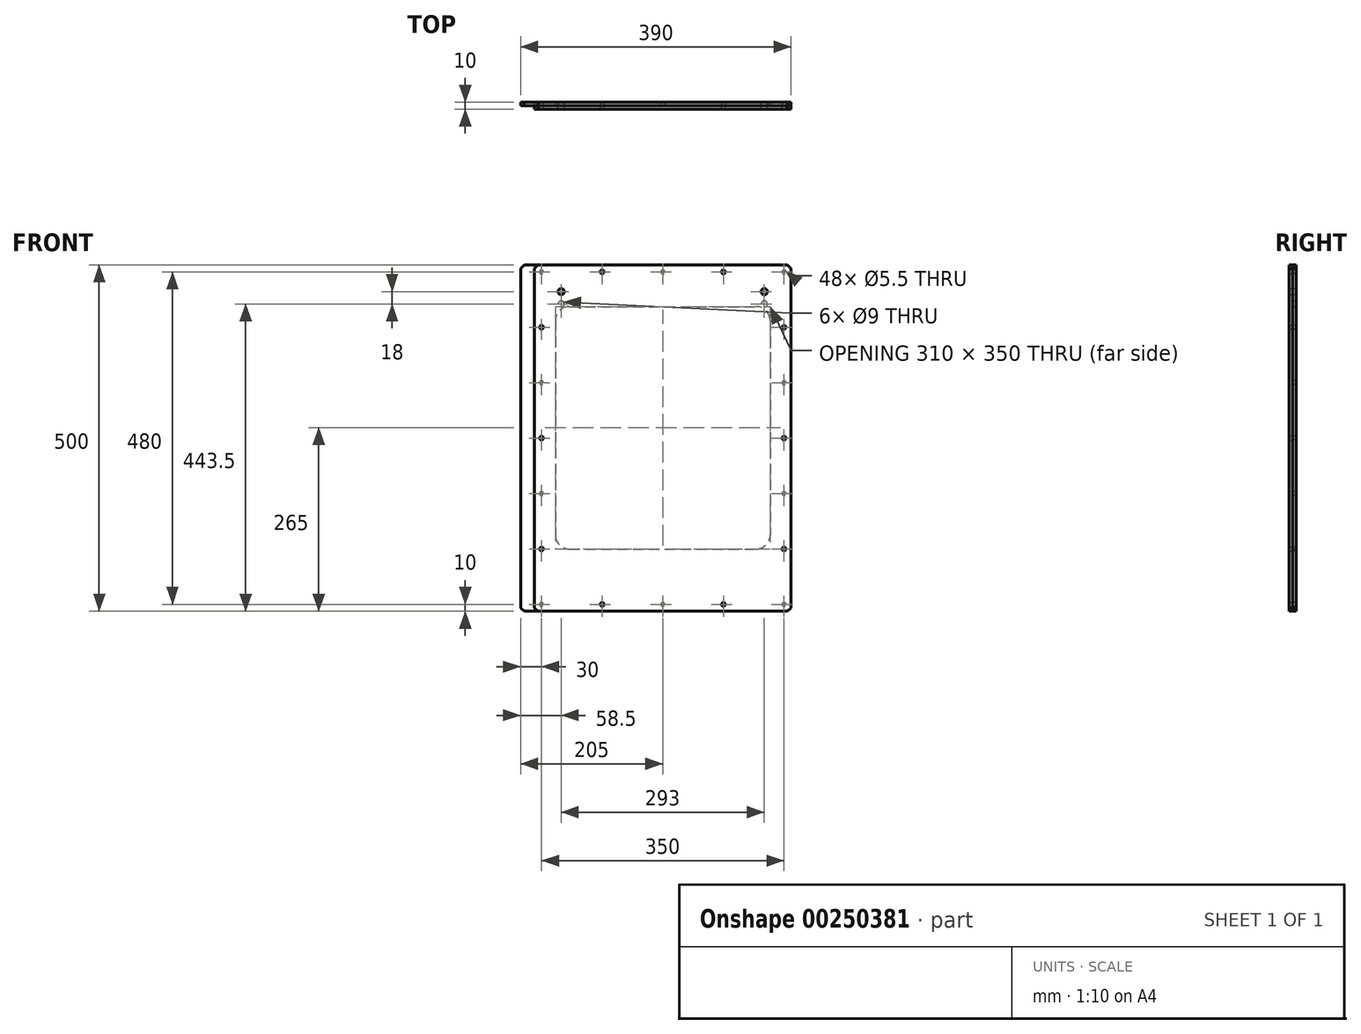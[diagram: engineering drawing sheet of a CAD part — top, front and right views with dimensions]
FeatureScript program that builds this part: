
annotation { "Feature Type Name" : "Feature", "Feature Type Description" : "" }
export const myFeature = defineFeature(function(context is Context, id is Id, definition is map)
    precondition{}
    {
        {
            var Q0;
            Q0=qCreatedBy(makeId("Front.planeOp"),FACE);
            var sketch = newSketch(context, id + "F0", { "sketchPlane" : qUnion([Q0])});
            skLineSegment(sketch, "E0.bottom", {"start": v(-175, 240) * mm, "end": v(175, 240) * mm, "construction": true});
            skLineSegment(sketch, "E0.top", {"start": v(-175, -240) * mm, "end": v(175, -240) * mm, "construction": true});
            skLineSegment(sketch, "E0.left", {"start": v(-175, 240) * mm, "end": v(-175, -240) * mm, "construction": true});
            skLineSegment(sketch, "E0.right", {"start": v(175, 240) * mm, "end": v(175, -240) * mm, "construction": true});
            skPoint(sketch, "E1", {"position": v(-175, 240) * mm});
            skPoint(sketch, "E2", {"position": v(175, 240) * mm});
            skPoint(sketch, "E3", {"position": v(-175, -240) * mm});
            skPoint(sketch, "E4", {"position": v(175, -240) * mm});
            skPoint(sketch, "E5.0.1.0", {"position": v(-175, -160) * mm});
            skPoint(sketch, "E5.0.2.0", {"position": v(-175, -80) * mm});
            skPoint(sketch, "E5.0.3.0", {"position": v(-175, 0) * mm});
            skPoint(sketch, "E5.0.4.0", {"position": v(-175, 80) * mm});
            skPoint(sketch, "E5.0.5.0", {"position": v(-175, 160) * mm});
            skPoint(sketch, "E5.1.1.0", {"position": v(175, -160) * mm});
            skPoint(sketch, "E5.1.2.0", {"position": v(175, -80) * mm});
            skPoint(sketch, "E5.1.3.0", {"position": v(175, 0) * mm});
            skPoint(sketch, "E5.1.4.0", {"position": v(175, 80) * mm});
            skPoint(sketch, "E5.1.5.0", {"position": v(175, 160) * mm});
            skLineSegment(sketch, "E5.direction2", {"start": v(-175, -240) * mm, "end": v(-175, -160) * mm, "construction": true});
            skPoint(sketch, "E6.1.0.0", {"position": v(-87.5, -240) * mm});
            skPoint(sketch, "E6.1.1.0", {"position": v(-87.5, 240) * mm});
            skPoint(sketch, "E6.2.0.0", {"position": v(0, -240) * mm});
            skPoint(sketch, "E6.2.1.0", {"position": v(0, 240) * mm});
            skPoint(sketch, "E6.3.0.0", {"position": v(87.5, -240) * mm});
            skPoint(sketch, "E6.3.1.0", {"position": v(87.5, 240) * mm});
            skLineSegment(sketch, "E6.direction1", {"start": v(-175, -240) * mm, "end": v(-87.5, -240) * mm, "construction": true});
            skLineSegment(sketch, "E6.direction2", {"start": v(-175, -240) * mm, "end": v(-175, 240) * mm, "construction": true});
            skSolve(sketch);
        }
        {
            var Q0;
            Q0=qCreatedBy(makeId("Front.planeOp"),FACE);
            var sketch = newSketch(context, id + "F1", { "sketchPlane" : qUnion([Q0])});
            skLineSegment(sketch, "E7.bottom", {"start": v(-205, 250) * mm, "end": v(185, 250) * mm});
            skLineSegment(sketch, "E7.top", {"start": v(-205, -250) * mm, "end": v(185, -250) * mm});
            skLineSegment(sketch, "E7.left", {"start": v(-205, 250) * mm, "end": v(-205, -250) * mm});
            skLineSegment(sketch, "E7.right", {"start": v(185, 250) * mm, "end": v(185, -250) * mm});
            skCircle(sketch, "E8", {"center": v(146.5, 193.5) * mm, "radius": 4.5 * mm});
            skCircle(sketch, "E9", {"center": v(-146.5, 193.5) * mm, "radius": 4.5 * mm});
            skSolve(sketch);
        }
        {
            var Q0;
            Q0=makeQuery(id+"F1.imprint","IMPRINT",FACE,{"disambiguationData":[TD([[makeQuery(id+"F1.imprint","IMPRINT",EDGE,{"derivedFrom":sQuery(id+"F1.wireOp",EDGE,"E7.bottom")}),-1.0]])]});
            extrude(context, id + "F2", {"entities" : qUnion([Q0]), "oppositeDirection" : true, "depth" : 5 * mm});
        }
        {
            var Q0;
            Q0=sQuery(id+"F0.wireOp",VERTEX,"E1");
            var Q1;
            Q1=sQuery(id+"F0.wireOp",VERTEX,"E5.0.5.0");
            var Q2;
            Q2=sQuery(id+"F0.wireOp",VERTEX,"E5.0.4.0");
            var Q3;
            Q3=sQuery(id+"F0.wireOp",VERTEX,"E5.0.2.0");
            var Q4;
            Q4=sQuery(id+"F0.wireOp",VERTEX,"E5.0.1.0");
            var Q5;
            Q5=sQuery(id+"F0.wireOp",VERTEX,"E3");
            var Q6;
            Q6=sQuery(id+"F0.wireOp",VERTEX,"E6.1.0.0");
            var Q7;
            Q7=sQuery(id+"F0.wireOp",VERTEX,"E6.3.0.0");
            var Q8;
            Q8=sQuery(id+"F0.wireOp",VERTEX,"E4");
            var Q9;
            Q9=sQuery(id+"F0.wireOp",VERTEX,"E5.1.1.0");
            var Q10;
            Q10=sQuery(id+"F0.wireOp",VERTEX,"E5.1.2.0");
            var Q11;
            Q11=sQuery(id+"F0.wireOp",VERTEX,"E5.1.4.0");
            var Q12;
            Q12=sQuery(id+"F0.wireOp",VERTEX,"E5.1.5.0");
            var Q13;
            Q13=sQuery(id+"F0.wireOp",VERTEX,"E2");
            var Q14;
            Q14=sQuery(id+"F0.wireOp",VERTEX,"E6.3.1.0");
            var Q15;
            Q15=sQuery(id+"F0.wireOp",VERTEX,"E6.2.1.0");
            var Q16;
            Q16=sQuery(id+"F0.wireOp",VERTEX,"E6.1.1.0");
            var Q17;
            Q17=sQuery(id+"F0.wireOp",VERTEX,"E5.0.3.0");
            var Q18;
            Q18=sQuery(id+"F0.wireOp",VERTEX,"E5.1.3.0");
            var Q19;
            Q19=makeQuery(id+"F2.opExtrude","SWEPT_BODY",BODY,{"disambiguationData":[OSD([sQuery(id+"F1.wireOp",EDGE,"E7.bottom"),sQuery(id+"F1.wireOp",EDGE,"E7.top"),sQuery(id+"F1.wireOp",EDGE,"E7.left"),sQuery(id+"F1.wireOp",EDGE,"E7.right"),sQuery(id+"F1.wireOp",EDGE,"E8"),sQuery(id+"F1.wireOp",EDGE,"E9")])]});
            hole(context, id + "F3", {"style" : HoleStyle.SIMPLE, "endStyle" : HoleEndStyle.BLIND, "holeDiameter" : 5.5 * mm, "holeDepth" : 17 * mm, "tappedDepth" : 12 * mm, "tapClearance" : 3, "locations" : qUnion([Q0, Q1, Q2, Q3, Q4, Q5, Q6, Q7, Q8, Q9, Q10, Q11, Q12, Q13, Q14, Q15, Q16, Q17, Q18]), "scope" : qUnion([Q19])});
        }
        {
            var Q0;
            Q0=qCreatedBy(makeId("Front.planeOp"),FACE);
            var sketch = newSketch(context, id + "F4", { "sketchPlane" : qUnion([Q0])});
            skLineSegment(sketch, "E10.bottom", {"start": v(-185, 250) * mm, "end": v(185, 250) * mm});
            skLineSegment(sketch, "E10.top", {"start": v(-185, -250) * mm, "end": v(185, -250) * mm});
            skLineSegment(sketch, "E10.left", {"start": v(-185, 250) * mm, "end": v(-185, -250) * mm});
            skLineSegment(sketch, "E10.right", {"start": v(185, 250) * mm, "end": v(185, -250) * mm});
            skLineSegment(sketch, "E11.bottom", {"start": v(-135, 190) * mm, "end": v(135, 190) * mm});
            skLineSegment(sketch, "E11.top", {"start": v(-135, -160) * mm, "end": v(135, -160) * mm});
            skLineSegment(sketch, "E11.left", {"start": v(-155, 170) * mm, "end": v(-155, -140) * mm});
            skLineSegment(sketch, "E11.right", {"start": v(155, 170) * mm, "end": v(155, -140) * mm});
            skCircle(sketch, "E12", {"center": v(-146.5, 211.5) * mm, "radius": 4.5 * mm});
            skCircle(sketch, "E13", {"center": v(146.5, 211.5) * mm, "radius": 4.5 * mm});
            skPoint(sketch, "E14.visualSharp", {"position": v(-155, 190) * mm});
            skArc(sketch, "E14.filletArc", {"start": v(-135, 190) * mm, "mid": v(-149.14, 184.14) * mm, "end": v(-155, 170) * mm});
            skPoint(sketch, "E15.visualSharp", {"position": v(155, 190) * mm});
            skArc(sketch, "E15.filletArc", {"start": v(155, 170) * mm, "mid": v(149.14, 184.14) * mm, "end": v(135, 190) * mm});
            skPoint(sketch, "E16.visualSharp", {"position": v(155, -160) * mm});
            skArc(sketch, "E16.filletArc", {"start": v(135, -160) * mm, "mid": v(149.14, -154.14) * mm, "end": v(155, -140) * mm});
            skPoint(sketch, "E17.visualSharp", {"position": v(-155, -160) * mm});
            skArc(sketch, "E17.filletArc", {"start": v(-155, -140) * mm, "mid": v(-149.14, -154.14) * mm, "end": v(-135, -160) * mm});
            skSolve(sketch);
        }
        {
            var Q0;
            Q0=makeQuery(id+"F4.imprint","IMPRINT",FACE,{"disambiguationData":[TD([[makeQuery(id+"F4.imprint","IMPRINT",EDGE,{"derivedFrom":sQuery(id+"F4.wireOp",EDGE,"E10.bottom")}),-1.0]])]});
            extrude(context, id + "F5", {"entities" : qUnion([Q0]), "oppositeDirection" : true, "depth" : 5 * mm});
        }
        {
            var Q0;
            Q0=sQuery(id+"F0.wireOp",VERTEX,"E5.1.4.0");
            var Q1;
            Q1=sQuery(id+"F0.wireOp",VERTEX,"E6.1.0.0");
            var Q2;
            Q2=sQuery(id+"F0.wireOp",VERTEX,"E0.right.start");
            var Q3;
            Q3=sQuery(id+"F0.wireOp",VERTEX,"E5.0.1.0");
            var Q4;
            Q4=sQuery(id+"F0.wireOp",VERTEX,"E5.1.1.0");
            var Q5;
            Q5=sQuery(id+"F0.wireOp",VERTEX,"E6.3.0.0");
            var Q6;
            Q6=sQuery(id+"F0.wireOp",VERTEX,"E6.2.1.0");
            var Q7;
            Q7=sQuery(id+"F0.wireOp",VERTEX,"E0.top.end");
            var Q8;
            Q8=sQuery(id+"F0.wireOp",VERTEX,"E6.direction1.start");
            var Q9;
            Q9=sQuery(id+"F0.wireOp",VERTEX,"E5.1.2.0");
            var Q10;
            Q10=sQuery(id+"F0.wireOp",VERTEX,"E5.0.4.0");
            var Q11;
            Q11=sQuery(id+"F0.wireOp",VERTEX,"E6.3.1.0");
            var Q12;
            Q12=sQuery(id+"F0.wireOp",VERTEX,"E5.1.5.0");
            var Q13;
            Q13=sQuery(id+"F0.wireOp",VERTEX,"E5.0.2.0");
            var Q14;
            Q14=sQuery(id+"F0.wireOp",VERTEX,"E6.1.1.0");
            var Q15;
            Q15=sQuery(id+"F0.wireOp",VERTEX,"E0.bottom.start");
            var Q16;
            Q16=sQuery(id+"F0.wireOp",VERTEX,"E5.1.3.0");
            var Q17;
            Q17=sQuery(id+"F0.wireOp",VERTEX,"E5.0.5.0");
            var Q18;
            Q18=sQuery(id+"F0.wireOp",VERTEX,"E5.0.3.0");
            var Q19;
            Q19=sQuery(id+"F0.wireOp",VERTEX,"E6.2.0.0");
            var Q20;
            Q20=makeQuery(id+"F5.opExtrude","SWEPT_BODY",BODY,{"disambiguationData":[OSD([sQuery(id+"F4.wireOp",EDGE,"E10.bottom"),sQuery(id+"F4.wireOp",EDGE,"E10.top"),sQuery(id+"F4.wireOp",EDGE,"E10.left"),sQuery(id+"F4.wireOp",EDGE,"E10.right"),sQuery(id+"F4.wireOp",EDGE,"E11.bottom"),sQuery(id+"F4.wireOp",EDGE,"E11.top"),sQuery(id+"F4.wireOp",EDGE,"E11.left"),sQuery(id+"F4.wireOp",EDGE,"E11.right"),sQuery(id+"F4.wireOp",EDGE,"E12"),sQuery(id+"F4.wireOp",EDGE,"E13"),sQuery(id+"F4.wireOp",EDGE,"E14.filletArc"),sQuery(id+"F4.wireOp",EDGE,"E15.filletArc"),sQuery(id+"F4.wireOp",EDGE,"E16.filletArc"),sQuery(id+"F4.wireOp",EDGE,"E17.filletArc")])]});
            hole(context, id + "F6", {"style" : HoleStyle.SIMPLE, "endStyle" : HoleEndStyle.BLIND, "holeDiameter" : 5.5 * mm, "holeDepth" : 17 * mm, "tappedDepth" : 12 * mm, "tapClearance" : 3, "locations" : qUnion([Q0, Q1, Q2, Q3, Q4, Q5, Q6, Q7, Q8, Q9, Q10, Q11, Q12, Q13, Q14, Q15, Q16, Q17, Q18, Q19]), "scope" : qUnion([Q20])});
        }
        {
            var Q0;
            Q0=makeQuery(id+"F4.imprint","IMPRINT",FACE,{"disambiguationData":[TD([[makeQuery(id+"F4.imprint","IMPRINT",EDGE,{"derivedFrom":sQuery(id+"F4.wireOp",EDGE,"E10.bottom")}),-1.0]])]});
            var Q1;
            Q1=makeQuery(id+"F4.imprint","IMPRINT",FACE,{"disambiguationData":[TD([[makeQuery(id+"F4.imprint","IMPRINT",EDGE,{"derivedFrom":sQuery(id+"F4.wireOp",EDGE,"E11.bottom")}),-1.0]])]});
            extrude(context, id + "F7", {"entities" : qUnion([Q0, Q1]), "depth" : 5 * mm});
        }
        {
            var Q0;
            Q0=sQuery(id+"F0.wireOp",VERTEX,"E5.0.5.0");
            var Q1;
            Q1=sQuery(id+"F0.wireOp",VERTEX,"E6.1.1.0");
            var Q2;
            Q2=sQuery(id+"F0.wireOp",VERTEX,"E6.3.1.0");
            var Q3;
            Q3=sQuery(id+"F0.wireOp",VERTEX,"E5.1.5.0");
            var Q4;
            Q4=sQuery(id+"F0.wireOp",VERTEX,"E5.0.1.0");
            var Q5;
            Q5=sQuery(id+"F0.wireOp",VERTEX,"E6.1.0.0");
            var Q6;
            Q6=sQuery(id+"F0.wireOp",VERTEX,"E6.3.0.0");
            var Q7;
            Q7=sQuery(id+"F0.wireOp",VERTEX,"E5.1.1.0");
            var Q8;
            Q8=sQuery(id+"F0.wireOp",VERTEX,"E5.0.3.0");
            var Q9;
            Q9=sQuery(id+"F0.wireOp",VERTEX,"E5.1.3.0");
            var Q10;
            Q10=makeQuery(id+"F7.opExtrude","SWEPT_BODY",BODY,{"disambiguationData":[OSD([sQuery(id+"F4.wireOp",EDGE,"E10.bottom"),sQuery(id+"F4.wireOp",EDGE,"E10.top"),sQuery(id+"F4.wireOp",EDGE,"E10.left"),sQuery(id+"F4.wireOp",EDGE,"E10.right"),sQuery(id+"F4.wireOp",EDGE,"E12"),sQuery(id+"F4.wireOp",EDGE,"E13")])]});
            hole(context, id + "F8", {"style" : HoleStyle.SIMPLE, "endStyle" : HoleEndStyle.BLIND, "oppositeDirection" : true, "standardTappedOrClearance" : lookupTablePath({ "standard" : "ISO", "fit" : "Normal", "size" : "M5", "type" : "Clearance" }), "standardBlindInLast" : lookupTablePath({ "fit" : "Standard", "standard" : "ISO", "size" : "M5", "type" : "Clearance" }), "holeDiameter" : 5.5 * mm, "holeDepth" : 22.4 * mm, "tappedDepth" : 20 * mm, "tapClearance" : 3, "locations" : qUnion([Q0, Q1, Q2, Q3, Q4, Q5, Q6, Q7, Q8, Q9]), "scope" : qUnion([Q10])});
        }
        {
            var Q0;
            Q0=makeQuery(id+"F7.opExtrude","SWEPT_EDGE",EDGE,{"disambiguationData":[OSD([sQuery(id+"F4.wireOp",EDGE,"E10.bottom"),sQuery(id+"F4.wireOp",EDGE,"E10.left")])]});
            var Q1;
            Q1=makeQuery(id+"F7.opExtrude","SWEPT_EDGE",EDGE,{"disambiguationData":[OSD([sQuery(id+"F4.wireOp",EDGE,"E10.bottom"),sQuery(id+"F4.wireOp",EDGE,"E10.right")])]});
            var Q2;
            Q2=makeQuery(id+"F7.opExtrude","SWEPT_EDGE",EDGE,{"disambiguationData":[OSD([sQuery(id+"F4.wireOp",EDGE,"E10.top"),sQuery(id+"F4.wireOp",EDGE,"E10.right")])]});
            var Q3;
            Q3=makeQuery(id+"F7.opExtrude","SWEPT_EDGE",EDGE,{"disambiguationData":[OSD([sQuery(id+"F4.wireOp",EDGE,"E10.top"),sQuery(id+"F4.wireOp",EDGE,"E10.left")])]});
            chamfer(context, id + "F9", {"entities" : qUnion([Q0, Q1, Q2, Q3]), "width" : 5 * mm, "tangentPropagation" : true});
        }
        {
            var Q0;
            Q0=makeQuery(id+"F5.opExtrude","SWEPT_EDGE",EDGE,{"disambiguationData":[OSD([sQuery(id+"F4.wireOp",EDGE,"E10.top"),sQuery(id+"F4.wireOp",EDGE,"E10.left")])]});
            var Q1;
            Q1=makeQuery(id+"F5.opExtrude","SWEPT_EDGE",EDGE,{"disambiguationData":[OSD([sQuery(id+"F4.wireOp",EDGE,"E10.top"),sQuery(id+"F4.wireOp",EDGE,"E10.right")])]});
            var Q2;
            Q2=makeQuery(id+"F5.opExtrude","SWEPT_EDGE",EDGE,{"disambiguationData":[OSD([sQuery(id+"F4.wireOp",EDGE,"E10.bottom"),sQuery(id+"F4.wireOp",EDGE,"E10.right")])]});
            var Q3;
            Q3=makeQuery(id+"F5.opExtrude","SWEPT_EDGE",EDGE,{"disambiguationData":[OSD([sQuery(id+"F4.wireOp",EDGE,"E10.bottom"),sQuery(id+"F4.wireOp",EDGE,"E10.left")])]});
            chamfer(context, id + "F10", {"entities" : qUnion([Q0, Q1, Q2, Q3]), "width" : 5 * mm, "tangentPropagation" : true});
        }
        {
            var Q0;
            Q0=makeQuery(id+"F2.opExtrude","SWEPT_EDGE",EDGE,{"disambiguationData":[OSD([sQuery(id+"F1.wireOp",EDGE,"E7.bottom"),sQuery(id+"F1.wireOp",EDGE,"E7.left")])]});
            var Q1;
            Q1=makeQuery(id+"F2.opExtrude","SWEPT_EDGE",EDGE,{"disambiguationData":[OSD([sQuery(id+"F1.wireOp",EDGE,"E7.bottom"),sQuery(id+"F1.wireOp",EDGE,"E7.right")])]});
            var Q2;
            Q2=makeQuery(id+"F2.opExtrude","SWEPT_EDGE",EDGE,{"disambiguationData":[OSD([sQuery(id+"F1.wireOp",EDGE,"E7.top"),sQuery(id+"F1.wireOp",EDGE,"E7.right")])]});
            var Q3;
            Q3=makeQuery(id+"F2.opExtrude","SWEPT_EDGE",EDGE,{"disambiguationData":[OSD([sQuery(id+"F1.wireOp",EDGE,"E7.top"),sQuery(id+"F1.wireOp",EDGE,"E7.left")])]});
            chamfer(context, id + "F11", {"entities" : qUnion([Q0, Q1, Q2, Q3]), "width" : 5 * mm, "tangentPropagation" : true});
        }
    });
